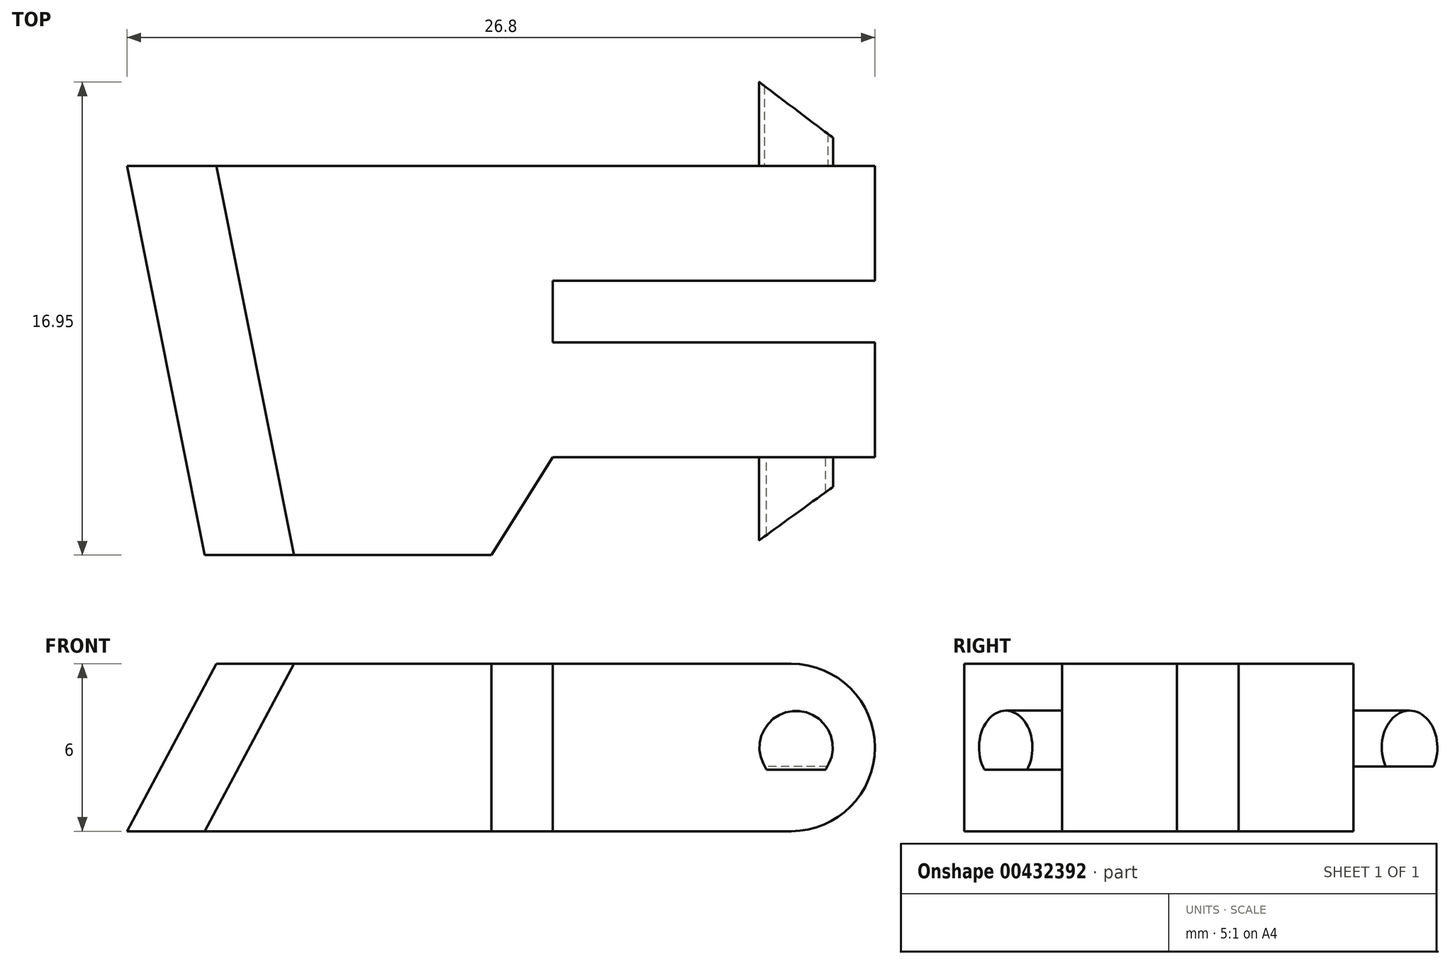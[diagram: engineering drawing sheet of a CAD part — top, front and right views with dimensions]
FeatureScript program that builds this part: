
annotation { "Feature Type Name" : "Feature", "Feature Type Description" : "" }
export const myFeature = defineFeature(function(context is Context, id is Id, definition is map)
    precondition{}
    {
        {
            var Q0;
            Q0=qCreatedBy(makeId("Top.planeOp"),FACE);
            var sketch = newSketch(context, id + "F0", { "sketchPlane" : qUnion([Q0])});
            skLineSegment(sketch, "E0", {"start": v(-35, 13.95) * mm, "end": v(-35, 9.83) * mm});
            skLineSegment(sketch, "E1", {"start": v(-35, 9.83) * mm, "end": v(-46.55, 9.83) * mm});
            skLineSegment(sketch, "E2", {"start": v(-46.55, 9.83) * mm, "end": v(-46.55, 7.62) * mm});
            skLineSegment(sketch, "E3", {"start": v(-46.55, 7.62) * mm, "end": v(-35, 7.62) * mm});
            skLineSegment(sketch, "E4", {"start": v(-35, 7.62) * mm, "end": v(-35, 3.5) * mm});
            skLineSegment(sketch, "E5", {"start": v(-35, 3.5) * mm, "end": v(-46.55, 3.5) * mm});
            skLineSegment(sketch, "E6", {"start": v(-35, 13.95) * mm, "end": v(-46.55, 13.95) * mm});
            skLineSegment(sketch, "E7", {"start": v(-46.55, 13.95) * mm, "end": v(-61.8, 13.95) * mm});
            skLineSegment(sketch, "E8", {"start": v(-61.8, 13.95) * mm, "end": v(-59.15, 0) * mm});
            skLineSegment(sketch, "E9", {"start": v(-59.15, 0) * mm, "end": v(-48.75, 0) * mm});
            skLineSegment(sketch, "E10", {"start": v(-48.75, 0) * mm, "end": v(-46.55, 3.5) * mm});
            skSolve(sketch);
        }
        {
            var Q0;
            Q0=makeQuery(id+"F0.imprint","IMPRINT",FACE,{"disambiguationData":[TD([[makeQuery(id+"F0.imprint","IMPRINT",EDGE,{"derivedFrom":sQuery(id+"F0.wireOp",EDGE,"E0")}),-1.0]])]});
            extrude(context, id + "F1", {"entities" : qUnion([Q0]), "depth" : 6 * mm});
        }
        {
            var Q0;
            Q0=makeQuery(id+"F1.opExtrude","SWEPT_FACE",FACE,{"disambiguationData":[OSD([sQuery(id+"F0.wireOp",EDGE,"E6"),sQuery(id+"F0.wireOp",EDGE,"E7")])]});
            var sketch = newSketch(context, id + "F2", { "sketchPlane" : qUnion([Q0])});
            skLineSegment(sketch, "E11", {"start": v(61.8, 0) * mm, "end": v(58.6, 6) * mm});
            skLineSegment(sketch, "E12", {"start": v(61.8, 0) * mm, "end": v(61.8, 6) * mm});
            skLineSegment(sketch, "E13", {"start": v(61.8, 6) * mm, "end": v(58.6, 6) * mm});
            skSolve(sketch);
        }
        {
            var Q0;
            Q0 = qSketchRegion(id + "F2", true);
            extrude(context, id + "F3", {"entities" : qUnion([Q0]), "operationType" : NewBodyOperationType.REMOVE, "oppositeDirection" : true, "depth" : 21.9 * mm, "hasDraft" : true, "draftAngle" : 10 * degree});
        }
        {
            var Q0;
            Q0=makeQuery(id+"F1.opExtrude","SWEPT_FACE",FACE,{"disambiguationData":[OSD([sQuery(id+"F0.wireOp",EDGE,"E5")])]});
            var sketch = newSketch(context, id + "F4", { "sketchPlane" : qUnion([Q0])});
            skCircle(sketch, "E14", {"center": v(-37.82, 3) * mm, "radius": 1.32 * mm});
            skSolve(sketch);
        }
        {
            var Q0;
            Q0=makeQuery(id+"F1.opExtrude","SWEPT_FACE",FACE,{"disambiguationData":[OSD([sQuery(id+"F0.wireOp",EDGE,"E6"),sQuery(id+"F0.wireOp",EDGE,"E7")])]});
            var sketch = newSketch(context, id + "F5", { "sketchPlane" : qUnion([Q0])});
            skCircle(sketch, "E15", {"center": v(37.82, 3) * mm, "radius": 1.32 * mm});
            skSolve(sketch);
        }
        {
            var Q0;
            Q0=makeQuery(id+"F5.imprint","IMPRINT",FACE,{"disambiguationData":[TD([[makeQuery(id+"F5.imprint","IMPRINT",EDGE,{"derivedFrom":sQuery(id+"F5.wireOp",EDGE,"E15")}),1.0]])]});
            extrude(context, id + "F6", {"entities" : qUnion([Q0]), "operationType" : NewBodyOperationType.ADD, "depth" : 3 * mm});
        }
        {
            var Q0;
            Q0 = qSketchRegion(id + "F4", true);
            extrude(context, id + "F7", {"entities" : qUnion([Q0]), "operationType" : NewBodyOperationType.ADD, "depth" : 3 * mm});
        }
        {
            var Q0;
            Q0=makeQuery(id+"F1.opExtrude","CAP_FACE",FACE,{"disambiguationData":[OSD([sQuery(id+"F0.wireOp",EDGE,"E0"),sQuery(id+"F0.wireOp",EDGE,"E1"),sQuery(id+"F0.wireOp",EDGE,"E2"),sQuery(id+"F0.wireOp",EDGE,"E3"),sQuery(id+"F0.wireOp",EDGE,"E4"),sQuery(id+"F0.wireOp",EDGE,"E5"),sQuery(id+"F0.wireOp",EDGE,"E6"),sQuery(id+"F0.wireOp",EDGE,"E7"),sQuery(id+"F0.wireOp",EDGE,"E8"),sQuery(id+"F0.wireOp",EDGE,"E9"),sQuery(id+"F0.wireOp",EDGE,"E10")])],"isStart":false});
            var sketch = newSketch(context, id + "F8", { "sketchPlane" : qUnion([Q0])});
            skLineSegment(sketch, "E16", {"start": v(-36.5, 0.5) * mm, "end": v(-36.5, 2.45) * mm});
            skLineSegment(sketch, "E17", {"start": v(-36.5, 2.45) * mm, "end": v(-39.2, 0.5) * mm});
            skLineSegment(sketch, "E18", {"start": v(-39.2, 0.5) * mm, "end": v(-36.5, 0.5) * mm});
            skSolve(sketch);
        }
        {
            var Q0;
            Q0=makeQuery(id+"F8.imprint","IMPRINT",FACE,{"disambiguationData":[TD([[makeQuery(id+"F8.imprint","IMPRINT",EDGE,{"derivedFrom":sQuery(id+"F8.wireOp",EDGE,"E16")}),1.0]])]});
            extrude(context, id + "F9", {"entities" : qUnion([Q0]), "operationType" : NewBodyOperationType.REMOVE, "oppositeDirection" : true, "depth" : 5.2 * mm});
        }
        {
            var Q0;
            Q0=makeQuery(id+"F1.opExtrude","CAP_FACE",FACE,{"disambiguationData":[OSD([sQuery(id+"F0.wireOp",EDGE,"E0"),sQuery(id+"F0.wireOp",EDGE,"E1"),sQuery(id+"F0.wireOp",EDGE,"E2"),sQuery(id+"F0.wireOp",EDGE,"E3"),sQuery(id+"F0.wireOp",EDGE,"E4"),sQuery(id+"F0.wireOp",EDGE,"E5"),sQuery(id+"F0.wireOp",EDGE,"E6"),sQuery(id+"F0.wireOp",EDGE,"E7"),sQuery(id+"F0.wireOp",EDGE,"E8"),sQuery(id+"F0.wireOp",EDGE,"E9"),sQuery(id+"F0.wireOp",EDGE,"E10")])],"isStart":false});
            var sketch = newSketch(context, id + "F10", { "sketchPlane" : qUnion([Q0])});
            skLineSegment(sketch, "E19", {"start": v(-39.15, 16.96) * mm, "end": v(-36.48, 16.96) * mm});
            skLineSegment(sketch, "E20", {"start": v(-36.48, 16.96) * mm, "end": v(-36.48, 14.95) * mm});
            skLineSegment(sketch, "E21", {"start": v(-36.48, 14.95) * mm, "end": v(-39.15, 16.96) * mm});
            skSolve(sketch);
        }
        {
            var Q0;
            Q0=makeQuery(id+"F10.imprint","IMPRINT",FACE,{"disambiguationData":[TD([[makeQuery(id+"F10.imprint","IMPRINT",EDGE,{"derivedFrom":sQuery(id+"F10.wireOp",EDGE,"E19")}),-1.0]])]});
            extrude(context, id + "F11", {"entities" : qUnion([Q0]), "operationType" : NewBodyOperationType.REMOVE, "oppositeDirection" : true, "depth" : 6.34 * mm});
        }
        {
            var Q0;
            Q0=makeQuery(id+"F1.opExtrude","CAP_EDGE",EDGE,{"disambiguationData":[OSD([sQuery(id+"F0.wireOp",EDGE,"E4")])],"isStart":false});
            var Q1;
            Q1=makeQuery(id+"F1.opExtrude","CAP_EDGE",EDGE,{"disambiguationData":[OSD([sQuery(id+"F0.wireOp",EDGE,"E4")])],"isStart":true});
            fillet(context, id + "F12", {"entities" : qUnion([Q0, Q1]), "radius" : 3 * mm, "tangentPropagation" : true, "allowEdgeOverflow" : false});
        }
        {
            var Q0;
            Q0=makeQuery(id+"F1.opExtrude","CAP_EDGE",EDGE,{"disambiguationData":[OSD([sQuery(id+"F0.wireOp",EDGE,"E0")])],"isStart":false});
            var Q1;
            Q1=makeQuery(id+"F1.opExtrude","CAP_EDGE",EDGE,{"disambiguationData":[OSD([sQuery(id+"F0.wireOp",EDGE,"E0")])],"isStart":true});
            fillet(context, id + "F13", {"entities" : qUnion([Q0, Q1]), "radius" : 3 * mm, "tangentPropagation" : true, "allowEdgeOverflow" : false});
        }
        {
            var Q0;
            Q0=makeQuery(id+"F1.opExtrude","SWEPT_FACE",FACE,{"disambiguationData":[OSD([sQuery(id+"F0.wireOp",EDGE,"E9")])]});
            var sketch = newSketch(context, id + "F14", { "sketchPlane" : qUnion([Q0])});
            skLineSegment(sketch, "E22.bottom", {"start": v(-36.52, 1.57) * mm, "end": v(-39.12, 1.57) * mm});
            skLineSegment(sketch, "E22.top", {"start": v(-36.52, 2.2) * mm, "end": v(-39.12, 2.2) * mm});
            skLineSegment(sketch, "E22.left", {"start": v(-36.52, 1.57) * mm, "end": v(-36.52, 2.2) * mm});
            skLineSegment(sketch, "E22.right", {"start": v(-39.12, 1.57) * mm, "end": v(-39.12, 2.2) * mm});
            skSolve(sketch);
        }
        {
            var Q0;
            Q0=makeQuery(id+"F14.imprint","IMPRINT",FACE,{"disambiguationData":[TD([[makeQuery(id+"F14.imprint","IMPRINT",EDGE,{"derivedFrom":sQuery(id+"F14.wireOp",EDGE,"E22.bottom")}),-1.0]])]});
            extrude(context, id + "F15", {"entities" : qUnion([Q0]), "operationType" : NewBodyOperationType.REMOVE, "oppositeDirection" : true, "depth" : 3.5 * mm});
        }
        {
            var Q0;
            Q0=makeQuery(id+"F1.opExtrude","SWEPT_FACE",FACE,{"disambiguationData":[OSD([sQuery(id+"F0.wireOp",EDGE,"E6"),sQuery(id+"F0.wireOp",EDGE,"E7")])]});
            var sketch = newSketch(context, id + "F16", { "sketchPlane" : qUnion([Q0])});
            skLineSegment(sketch, "E23.bottom", {"start": v(39.06, 1.65) * mm, "end": v(36.57, 1.65) * mm});
            skLineSegment(sketch, "E23.top", {"start": v(39.06, 2.32) * mm, "end": v(36.57, 2.32) * mm});
            skLineSegment(sketch, "E23.left", {"start": v(39.06, 1.65) * mm, "end": v(39.06, 2.32) * mm});
            skLineSegment(sketch, "E23.right", {"start": v(36.57, 1.65) * mm, "end": v(36.57, 2.32) * mm});
            skSolve(sketch);
        }
        {
            var Q0;
            Q0 = qSketchRegion(id + "F16", true);
            extrude(context, id + "F17", {"entities" : qUnion([Q0]), "operationType" : NewBodyOperationType.REMOVE, "depth" : 25 * mm});
        }
    });
